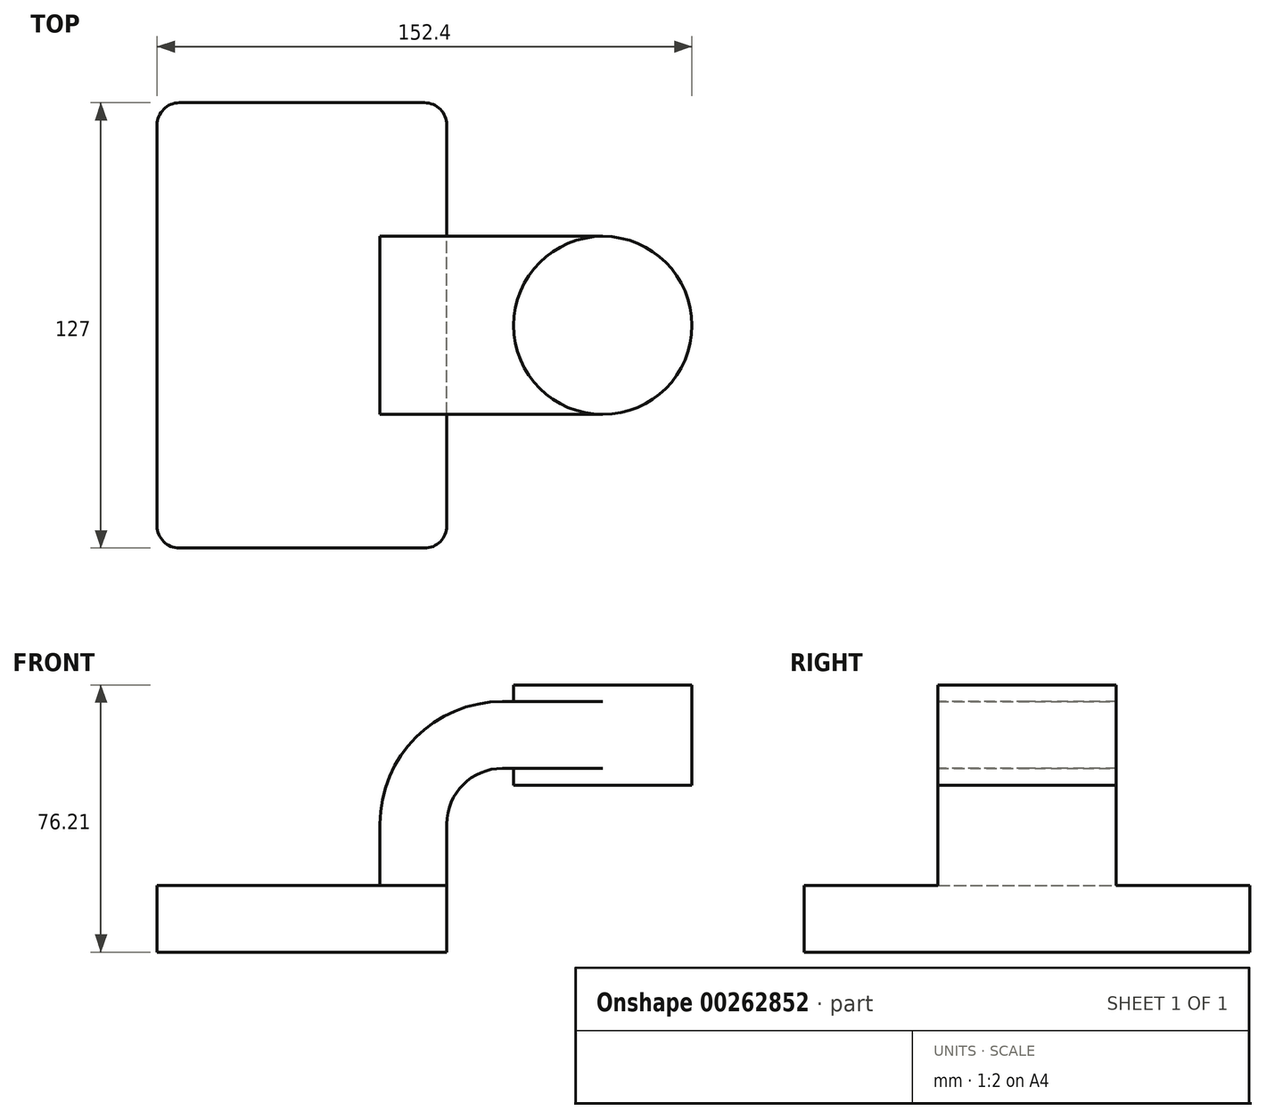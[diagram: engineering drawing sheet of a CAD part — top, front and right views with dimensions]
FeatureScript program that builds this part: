
annotation { "Feature Type Name" : "Feature", "Feature Type Description" : "" }
export const myFeature = defineFeature(function(context is Context, id is Id, definition is map)
    precondition{}
    {
        {
            var Q0;
            Q0=qCreatedBy(makeId("Front.planeOp"),FACE);
            var sketch = newSketch(context, id + "F0", { "sketchPlane" : qUnion([Q0])});
            skLineSegment(sketch, "E0.bottom", {"start": v(-41.28, 9.52) * mm, "end": v(41.27, 9.53) * mm});
            skLineSegment(sketch, "E0.top", {"start": v(-41.28, -9.53) * mm, "end": v(41.28, -9.53) * mm});
            skLineSegment(sketch, "E0.left", {"start": v(-41.28, 9.52) * mm, "end": v(-41.27, -9.53) * mm});
            skLineSegment(sketch, "E0.right", {"start": v(41.28, 9.53) * mm, "end": v(41.28, -9.52) * mm});
            skPoint(sketch, "E0.middle", {"position": v(0, 0) * mm});
            skLineSegment(sketch, "E1.bottom", {"start": v(60.32, 38.1) * mm, "end": v(111.12, 38.1) * mm});
            skLineSegment(sketch, "E1.top", {"start": v(60.32, 66.67) * mm, "end": v(111.12, 66.67) * mm});
            skLineSegment(sketch, "E1.left", {"start": v(60.32, 38.1) * mm, "end": v(60.32, 66.67) * mm});
            skLineSegment(sketch, "E1.right", {"start": v(111.12, 38.1) * mm, "end": v(111.12, 66.67) * mm});
            skPoint(sketch, "E1.middle", {"position": v(85.72, 52.39) * mm});
            skLineSegment(sketch, "E2", {"start": v(41.27, 9.53) * mm, "end": v(41.27, 27) * mm});
            skArc(sketch, "E3", {"start": v(41.27, 27) * mm, "mid": v(45.92, 38.23) * mm, "end": v(57.15, 42.88) * mm});
            skLineSegment(sketch, "E4", {"start": v(57.15, 42.88) * mm, "end": v(90.87, 42.88) * mm});
            skLineSegment(sketch, "E5.0", {"start": v(57.15, 61.93) * mm, "end": v(90.87, 61.93) * mm});
            skArc(sketch, "E5.1", {"start": v(22.22, 27) * mm, "mid": v(32.45, 51.7) * mm, "end": v(57.15, 61.93) * mm});
            skLineSegment(sketch, "E5.2", {"start": v(22.22, 9.53) * mm, "end": v(22.22, 27) * mm});
            skLineSegment(sketch, "E6", {"start": v(85.72, 38.1) * mm, "end": v(85.72, 66.67) * mm});
            skFitSpline(sketch, "E7", {"points": [v(-41.28, 9.52) * mm, v(57.15, 61.93) * mm], "startDerivative": vector(45.34, 94.45) * mm, "endDerivative": vector(149.91, -22.76) * mm});
            skSolve(sketch);
        }
        {
            var Q0;
            Q0=makeQuery(id+"F0.imprint","IMPRINT",FACE,{"disambiguationData":[TD([[makeQuery(id+"F0.imprint","IMPRINT",EDGE,{"derivedFrom":sQuery(id+"F0.wireOp",EDGE,"E0.top")}),1.0]])]});
            extrude(context, id + "F1", {"entities" : qUnion([Q0]), "depth" : 127 * mm, "symmetric" : true});
        }
        {
            var Q0;
            {var subQ1=sQuery(id+"F0.wireOp",EDGE,"E2");Q0=makeQuery(id+"F0.imprint","IMPRINT",FACE,{"disambiguationData":[TD([[makeQuery(id+"F0.imprint","IMPRINT",EDGE,{"derivedFrom":subQ1}),1.0]])]});}
            var Q1;
            {var subQ0=sQuery(id+"F0.wireOp",EDGE,"E4");var subQ1=sQuery(id+"F0.wireOp",EDGE,"E1.left");var subQ2=makeQuery(id+"F0.imprint","INTERSECT",VERTEX,{"derivedFrom":[subQ1,subQ0]});Q1=makeQuery(id+"F0.imprint","IMPRINT",FACE,{"disambiguationData":[TD([[makeQuery(id+"F0.imprint","IMPRINT",EDGE,{"disambiguationData":[TD([[subQ2,-1.0]])],"derivedFrom":subQ1}),-1.0]])]});}
            extrude(context, id + "F2", {"entities" : qUnion([Q0, Q1]), "operationType" : NewBodyOperationType.ADD, "depth" : 50.8 * mm, "symmetric" : true});
        }
        {
            var Q0;
            Q0=makeQuery(id+"F0.imprint","IMPRINT",FACE,{"disambiguationData":[TD([[makeQuery(id+"F0.imprint","IMPRINT",EDGE,{"derivedFrom":sQuery(id+"F0.wireOp",EDGE,"E5.1")}),1.0]])]});
            extrude(context, id + "F3", {"entities" : qUnion([Q0]), "operationType" : NewBodyOperationType.ADD, "depth" : 15.88 * mm, "symmetric" : true});
        }
        {
            var Q0;
            Q0=makeQuery(id+"F1.opExtrude","CAP_EDGE",EDGE,{"disambiguationData":[OSD([sQuery(id+"F0.wireOp",EDGE,"E0.right")])],"isStart":false});
            var Q1;
            Q1=makeQuery(id+"F1.opExtrude","CAP_EDGE",EDGE,{"disambiguationData":[OSD([sQuery(id+"F0.wireOp",EDGE,"E0.left")])],"isStart":false});
            var Q2;
            Q2=makeQuery(id+"F1.opExtrude","CAP_EDGE",EDGE,{"disambiguationData":[OSD([sQuery(id+"F0.wireOp",EDGE,"E0.left")])],"isStart":true});
            var Q3;
            Q3=makeQuery(id+"F1.opExtrude","CAP_EDGE",EDGE,{"disambiguationData":[OSD([sQuery(id+"F0.wireOp",EDGE,"E0.right")])],"isStart":true});
            fillet(context, id + "F4", {"entities" : qUnion([Q0, Q1, Q2, Q3]), "radius" : 6.35 * mm, "tangentPropagation" : true, "allowEdgeOverflow" : false});
        }
        {
            var Q0;
            {var subQ0=sQuery(id+"F0.wireOp",EDGE,"E1.right");Q0=makeQuery(id+"F0.imprint","IMPRINT",FACE,{"disambiguationData":[TD([[makeQuery(id+"F0.imprint","IMPRINT",EDGE,{"derivedFrom":subQ0}),1.0]])]});}
            var Q1;
            Q1=sQuery(id+"F0.wireOp",EDGE,"E6");
            revolve(context, id + "F5", {"operationType" : NewBodyOperationType.ADD, "entities" : qUnion([Q0]), "axis" : qUnion([Q1]), "revolveType" : RevolveType.FULL});
        }
    });
